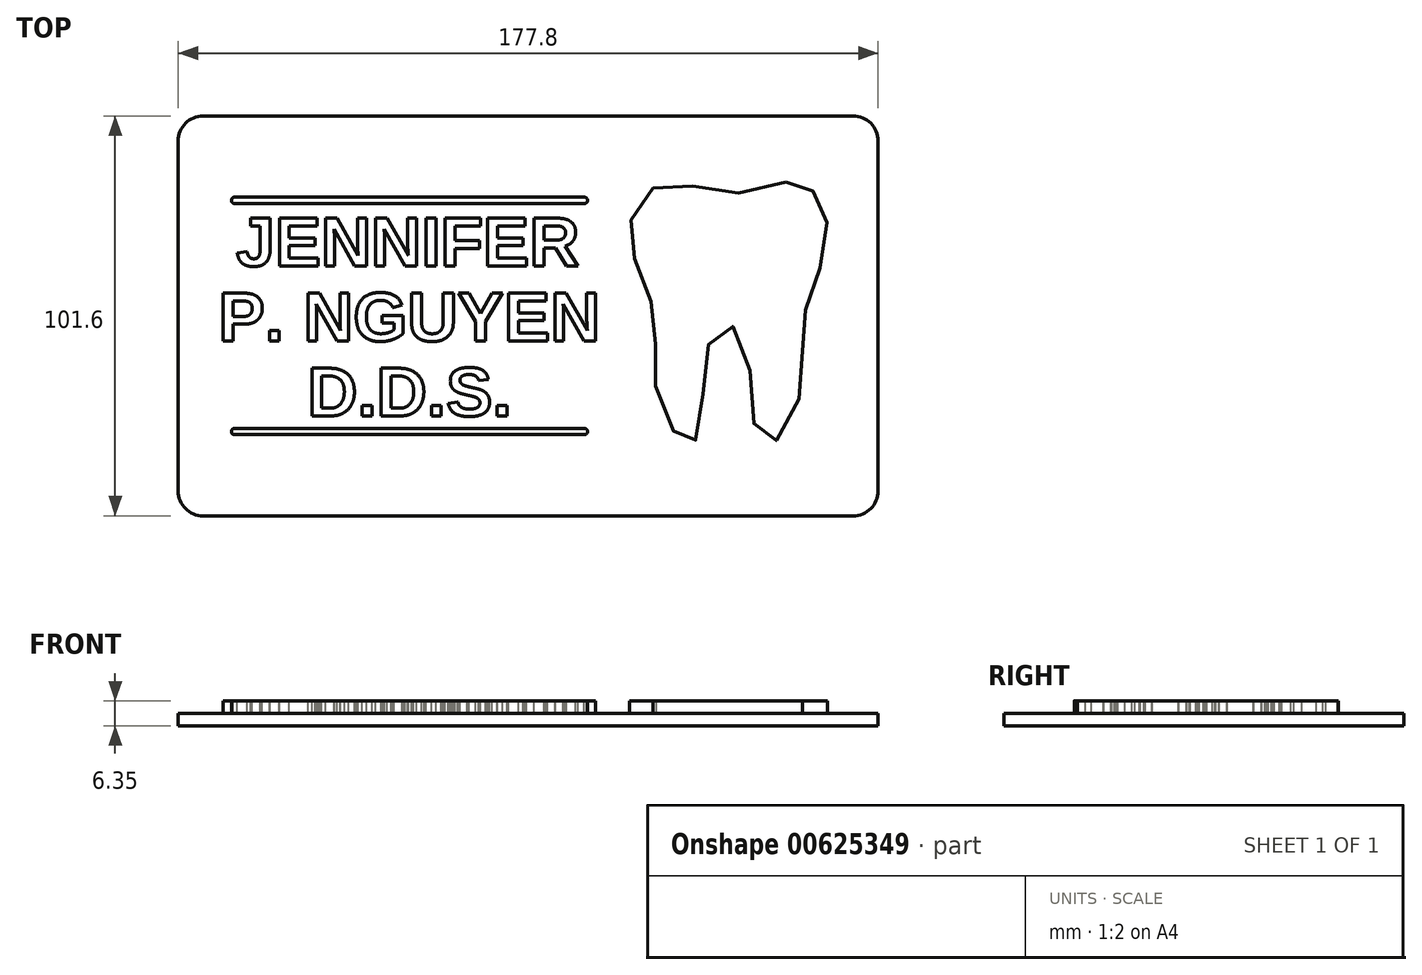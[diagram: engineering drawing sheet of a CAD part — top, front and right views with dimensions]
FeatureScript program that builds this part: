
annotation { "Feature Type Name" : "Feature", "Feature Type Description" : "" }
export const myFeature = defineFeature(function(context is Context, id is Id, definition is map)
    precondition{}
    {
        {
            var Q0;
            Q0=qCreatedBy(makeId("Top.planeOp"),FACE);
            var sketch = newSketch(context, id + "F0", { "sketchPlane" : qUnion([Q0])});
            skLineSegment(sketch, "E0.bottom", {"start": v(-82.55, 50.8) * mm, "end": v(82.55, 50.8) * mm});
            skLineSegment(sketch, "E0.top", {"start": v(-82.55, -50.8) * mm, "end": v(82.55, -50.8) * mm});
            skLineSegment(sketch, "E0.left", {"start": v(-88.9, 44.45) * mm, "end": v(-88.9, -44.45) * mm});
            skLineSegment(sketch, "E0.right", {"start": v(88.9, 44.45) * mm, "end": v(88.9, -44.45) * mm});
            skPoint(sketch, "E0.middle", {"position": v(0, 0) * mm});
            skPoint(sketch, "E1.visualSharp", {"position": v(-88.9, 50.8) * mm});
            skArc(sketch, "E1.filletArc", {"start": v(-82.55, 50.8) * mm, "mid": v(-87.04, 48.94) * mm, "end": v(-88.9, 44.45) * mm});
            skPoint(sketch, "E2.visualSharp", {"position": v(88.9, 50.8) * mm});
            skArc(sketch, "E2.filletArc", {"start": v(88.9, 44.45) * mm, "mid": v(87.04, 48.94) * mm, "end": v(82.55, 50.8) * mm});
            skPoint(sketch, "E3.visualSharp", {"position": v(88.9, -50.8) * mm});
            skArc(sketch, "E3.filletArc", {"start": v(82.55, -50.8) * mm, "mid": v(87.04, -48.94) * mm, "end": v(88.9, -44.45) * mm});
            skPoint(sketch, "E4.visualSharp", {"position": v(-88.9, -50.8) * mm});
            skArc(sketch, "E4.filletArc", {"start": v(-88.9, -44.45) * mm, "mid": v(-87.04, -48.94) * mm, "end": v(-82.55, -50.8) * mm});
            skSolve(sketch);
        }
        {
            var Q0;
            Q0 = qSketchRegion(id + "F0", true);
            extrude(context, id + "F1", {"entities" : qUnion([Q0]), "oppositeDirection" : true, "depth" : 6.35 * mm, "offsetDistance" : 25.4 * mm});
        }
        {
            var Q0;
            Q0=makeQuery(id+"F1.opExtrude","CAP_FACE",FACE,{"disambiguationData":[OSD([sQuery(id+"F0.wireOp",EDGE,"E0.bottom"),sQuery(id+"F0.wireOp",EDGE,"E0.top"),sQuery(id+"F0.wireOp",EDGE,"E0.left"),sQuery(id+"F0.wireOp",EDGE,"E0.right"),sQuery(id+"F0.wireOp",EDGE,"E1.filletArc"),sQuery(id+"F0.wireOp",EDGE,"E2.filletArc"),sQuery(id+"F0.wireOp",EDGE,"E3.filletArc"),sQuery(id+"F0.wireOp",EDGE,"E4.filletArc")])],"isStart":true});
            var sketch = newSketch(context, id + "F2", { "sketchPlane" : qUnion([Q0])});
            skText(sketch, "E5", { "text": "JENNIFER", "fontName": "Arimo-Bold.ttf"});
            skText(sketch, "E6", { "text": "P. NGUYEN", "fontName": "Arimo-Bold.ttf"});
            skText(sketch, "E7", { "text": "D.D.S.", "fontName": "Arimo-Bold.ttf"});
            skLineSegment(sketch, "E8", {"start": v(-30.16, 25.4) * mm, "end": v(-30.16, 50.8) * mm, "construction": true});
            skLineSegment(sketch, "E9", {"start": v(-30.16, -25.4) * mm, "end": v(-30.16, -50.8) * mm, "construction": true});
            skLineSegment(sketch, "E10", {"start": v(0, 0) * mm, "end": v(-4.14, 0) * mm, "construction": true});
            skFitSpline(sketch, "E11", {"points": [v(65.44, 34.05) * mm, v(50.55, 30.98) * mm, v(37.85, 33.83) * mm, v(29.09, 30.33) * mm, v(25.8, 21.13) * mm, v(28.43, 10.84) * mm, v(32.6, -2.3) * mm, v(31.71, -12.81) * mm, v(35.44, -26.6) * mm, v(40.91, -32.96) * mm, v(44.2, -25.51) * mm, v(45.3, -8.87) * mm, v(50.55, -2.08) * mm, v(56.02, -11.06) * mm, v(57.77, -28.8) * mm, v(62.15, -32.08) * mm, v(68.94, -20.7) * mm, v(69.6, -6.46) * mm, v(71.13, 4.05) * mm, v(75.5, 16.97) * mm, v(74.85, 28.58) * mm, v(70.91, 32.74) * mm, v(65.44, 34.05) * mm]});
            skLineSegment(sketch, "E12.0", {"start": v(-82.55, 50.8) * mm, "end": v(82.55, 50.8) * mm});
            skLineSegment(sketch, "E12.1", {"start": v(-82.55, -50.8) * mm, "end": v(82.55, -50.8) * mm});
            skLineSegment(sketch, "E12.2", {"start": v(-88.9, 44.45) * mm, "end": v(-88.9, -44.45) * mm});
            skLineSegment(sketch, "E12.3", {"start": v(88.9, 44.45) * mm, "end": v(88.9, -44.45) * mm});
            skPoint(sketch, "E12.4", {"position": v(0, 0) * mm});
            skPoint(sketch, "E12.5", {"position": v(-88.9, 50.8) * mm});
            skArc(sketch, "E12.6", {"start": v(-82.55, 50.8) * mm, "mid": v(-87.04, 48.94) * mm, "end": v(-88.9, 44.45) * mm});
            skPoint(sketch, "E12.7", {"position": v(88.9, 50.8) * mm});
            skArc(sketch, "E12.8", {"start": v(88.9, 44.45) * mm, "mid": v(87.04, 48.94) * mm, "end": v(82.55, 50.8) * mm});
            skPoint(sketch, "E12.9", {"position": v(88.9, -50.8) * mm});
            skArc(sketch, "E12.10", {"start": v(82.55, -50.8) * mm, "mid": v(87.04, -48.94) * mm, "end": v(88.9, -44.45) * mm});
            skPoint(sketch, "E12.11", {"position": v(-88.9, -50.8) * mm});
            skArc(sketch, "E12.12", {"start": v(-88.9, -44.45) * mm, "mid": v(-87.04, -48.94) * mm, "end": v(-82.55, -50.8) * mm});
            skLineSegment(sketch, "E13.bottom", {"start": v(-74.61, 30.16) * mm, "end": v(14.29, 30.16) * mm});
            skLineSegment(sketch, "E13.top", {"start": v(-74.61, 28.58) * mm, "end": v(14.29, 28.58) * mm});
            skLineSegment(sketch, "E13.left", {"start": v(-74.61, 30.16) * mm, "end": v(-74.61, 28.58) * mm, "construction": true});
            skLineSegment(sketch, "E13.right", {"start": v(14.29, 30.16) * mm, "end": v(14.29, 28.58) * mm, "construction": true});
            skPoint(sketch, "E13.middle", {"position": v(-30.16, 29.37) * mm});
            skArc(sketch, "E14", {"start": v(14.29, 28.58) * mm, "mid": v(15.08, 29.37) * mm, "end": v(14.29, 30.16) * mm});
            skArc(sketch, "E15", {"start": v(-74.61, 30.16) * mm, "mid": v(-75.4, 29.37) * mm, "end": v(-74.61, 28.58) * mm});
            skLineSegment(sketch, "E16.MirrorCS", {"start": v(-74.61, -28.58) * mm, "end": v(14.29, -28.58) * mm});
            skLineSegment(sketch, "E17.MirrorCS", {"start": v(-74.61, -30.16) * mm, "end": v(14.29, -30.16) * mm});
            skArc(sketch, "E18.MirrorCS", {"start": v(14.29, -28.58) * mm, "mid": v(15.08, -29.37) * mm, "end": v(14.29, -30.16) * mm});
            skArc(sketch, "E19.MirrorCS", {"start": v(-74.61, -30.16) * mm, "mid": v(-75.4, -29.37) * mm, "end": v(-74.61, -28.58) * mm});
            const initialGuessF2  = {"E5": [-0.0742, 0.0127, 1, 0, 0.0127], "E6": [-0.0787, -0.00635, 1, 0, 0.0127], "E7": [-0.05614, -0.0254, 1, 0, 0.0127]};
            skSetInitialGuess(sketch, initialGuessF2);
            skSolve(sketch);
        }
        {
            var Q0;
            Q0 = qSketchRegion(id + "F2", true);
            var Q1;
            Q1=makeQuery(id+"F2.imprint","IMPRINT",FACE,{"disambiguationData":[TD([[makeQuery(id+"F2.imprint","IMPRINT",EDGE,{"derivedFrom":sQuery(id+"F2.wireOp",EDGE,"E6.sketch_text.stroke-10")}),1.0]])]});
            var Q2;
            Q2=makeQuery(id+"F2.imprint","IMPRINT",FACE,{"disambiguationData":[TD([[makeQuery(id+"F2.imprint","IMPRINT",EDGE,{"derivedFrom":sQuery(id+"F2.wireOp",EDGE,"E7.sketch_text.stroke-8")}),1.0]])]});
            var Q3;
            Q3=makeQuery(id+"F2.imprint","IMPRINT",FACE,{"disambiguationData":[TD([[makeQuery(id+"F2.imprint","IMPRINT",EDGE,{"derivedFrom":sQuery(id+"F2.wireOp",EDGE,"E7.sketch_text.stroke-27")}),1.0]])]});
            var Q4;
            Q4=makeQuery(id+"F2.imprint","IMPRINT",FACE,{"disambiguationData":[TD([[makeQuery(id+"F2.imprint","IMPRINT",EDGE,{"derivedFrom":sQuery(id+"F2.wireOp",EDGE,"E5.sketch_text.stroke-88")}),1.0]])]});
            extrude(context, id + "F3", {"entities" : qUnion([Q0, Q1, Q2, Q3, Q4]), "operationType" : NewBodyOperationType.REMOVE, "oppositeDirection" : true, "depth" : 3.17 * mm, "offsetDistance" : 25.4 * mm});
        }
    });
